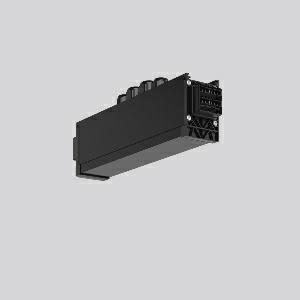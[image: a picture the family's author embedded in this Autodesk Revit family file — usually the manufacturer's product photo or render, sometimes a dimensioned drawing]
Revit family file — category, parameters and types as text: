
# Revit family: linedo_mitteleinspeisung_7pol_s_s_982698_013_5_ae7c
name_source: partatom
category: Lighting Fixtures
units: mm (PartAtom-declared; Revit-internal decimal feet)

## family parameters
Cut with Voids When Loaded = No
Host = Face
Light Source = No
Part Type = Normal
Room Calculation Point = No
Round Connector Dimension = Use Diameter
Shared = No

## types (1)
- LINEDO_Mitteleinspeisung_7pol_S_S
    Apparent Load = 0 VA
    Default Elevation = 1800 mm
    Description = Series: LINEDO
Middle power feed, 7-pole, connection plug / plug. Housing: extruded aluminium profile, powder-coated. Cover made of plastic, surface like housing. LINEDO plug system, plastic, black. 4 cable glands (2 x M20 and 2 x M25). Cable glands on top. Easy connection for rigid or flexible wires. Especially for use with continuous line modules with high opal diffuser.
Colour: black
Length: 349 mm
Width: 58 mm
Height: 91 mm
Weight: 801 g
    Height = 91 mm
    Lamp = 0 x
    Length = 349 mm
    Luminous efficacy = 0 lm/W
    Manufacturer = RZB
    ModVariant = No
    Model = 982698.013.5
    Mounting Place = Ceiling
    Mounting Type = Surface mounted
    Number of Poles = 1
    OnlyDefault = Yes
    Power Factor = 1
    Product Name = LINEDO_Mitteleinspeisung_7pol_S_S
    Product group = Surface mounted continuous line luminaire system
    ProductGroupID = 310
    Protection Class = Protection class I
    Protection Degree = Degree of protection
    RLX_Detail_Level = 1
    RLX_Emergency_Light_Flux = 0 lm
    RLX_Emergency_Type = 0
    RLX_Emergency_Type_DB = No
    RlxData = <blob elided: 24549 chars, md5=07fa54cc>
    Standby Power = 0 W
    System Light Flux = 0 lm
    System Power = 0 W
    Type Comments = Product without accessories
    Type Image = 982698.013.2.jpg
    URL = http://relux.com
    VarID = ---
    Voltage = 0 V
    Weight = 0.00 kg
    Width = 58 mm

## geometry (parser evidence)
native form markers: Blend x4, Sweep x11
no freeform markers — native parametric forms only
